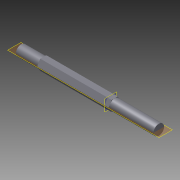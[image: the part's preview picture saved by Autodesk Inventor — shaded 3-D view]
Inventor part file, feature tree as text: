
AUTODESK INVENTOR PART (.ipt)
format: ipt  version: 2012 (Build 160160000, 160)  size: 137,216 bytes
history: native  units: in
note: dims shown in document units (in); Inventor stores cm internally (conversion verified against a paired STEP export)
features: other x6, plane x5, sketch x3
ambient origin geometry x8: Origin, YZ Plane, XZ Plane, XY Plane, X Axis, Y Axis, Z Axis, Center Point
bodies: Solid1 (feature_tree)
feature tree (14):
  other  "Shaft"
  other  "Solid1::Shaft"
  other  "Main Sketch"
  sketch  "Sketch4"  dims[d0=0.3937in]
  sketch  "Sketch5"  dims[d1=0.0in]
  sketch  "Sketch6"  dims[d2=0.0in]
  plane  "Work Plane1"
  plane  "Work Plane2"
  plane  "Work Plane3"
  plane  "Work Plane4"
  other  "Start Plane"
  plane  "XY Plane_1"
  other  "X Axis_1"
  other  "TaggingFeature1"
